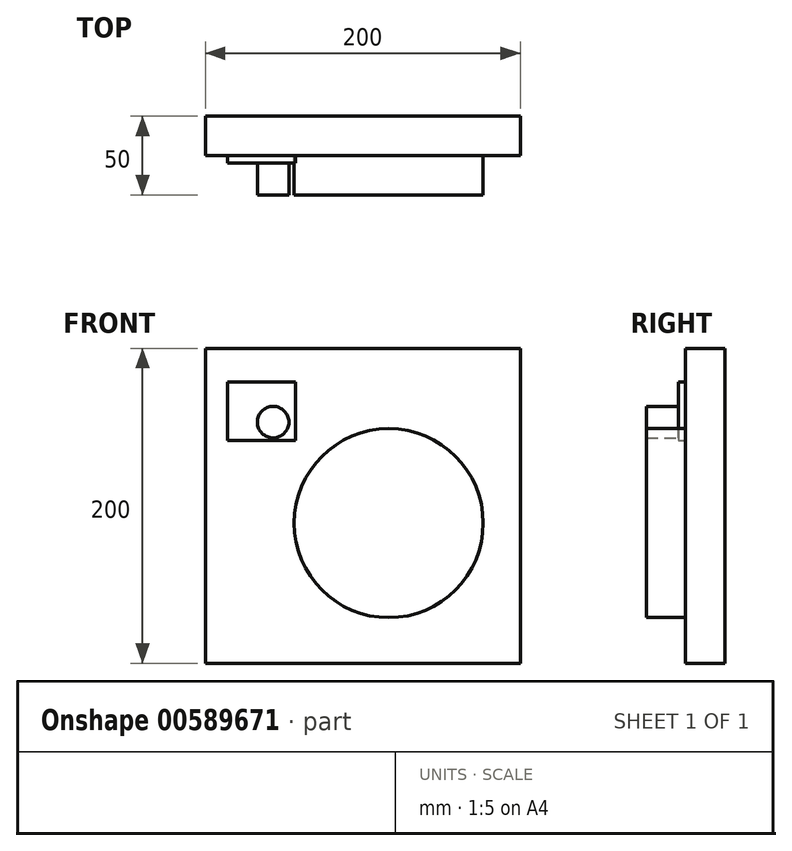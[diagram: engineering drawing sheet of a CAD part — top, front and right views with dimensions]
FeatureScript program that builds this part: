
annotation { "Feature Type Name" : "Feature", "Feature Type Description" : "" }
export const myFeature = defineFeature(function(context is Context, id is Id, definition is map)
    precondition{}
    {
        {
            var Q0;
            Q0=qCreatedBy(makeId("Front.planeOp"),FACE);
            var sketch = newSketch(context, id + "F0", { "sketchPlane" : qUnion([Q0])});
            skLineSegment(sketch, "E0.bottom", {"start": v(-200, -200) * mm, "end": v(0, -200) * mm});
            skLineSegment(sketch, "E0.top", {"start": v(-200, 0) * mm, "end": v(0, 0) * mm});
            skLineSegment(sketch, "E0.left", {"start": v(-200, -200) * mm, "end": v(-200, 0) * mm});
            skLineSegment(sketch, "E0.right", {"start": v(0, -200) * mm, "end": v(0, 0) * mm});
            skSolve(sketch);
        }
        {
            var Q0;
            Q0 = qSketchRegion(id + "F0", true);
            extrude(context, id + "F1", {"entities" : qUnion([Q0]), "depth" : 25 * mm, "offsetDistance" : 25 * mm});
        }
        {
            var Q0;
            Q0=makeQuery(id+"F1.opExtrude","CAP_FACE",FACE,{"disambiguationData":[OSD([sQuery(id+"F0.wireOp",EDGE,"E0.bottom"),sQuery(id+"F0.wireOp",EDGE,"E0.top"),sQuery(id+"F0.wireOp",EDGE,"E0.left"),sQuery(id+"F0.wireOp",EDGE,"E0.right")])],"isStart":false});
            var sketch = newSketch(context, id + "F2", { "sketchPlane" : qUnion([Q0])});
            skCircle(sketch, "E1", {"center": v(-156.98, -46.83) * mm, "radius": 10 * mm});
            skCircle(sketch, "E2", {"center": v(-83.56, -110.98) * mm, "radius": 60 * mm});
            skLineSegment(sketch, "E3", {"start": v(-156.98, -46.83) * mm, "end": v(-83.56, -110.98) * mm});
            skSolve(sketch);
        }
        {
            var Q0;
            Q0 = qSketchRegion(id + "F2", true);
            extrude(context, id + "F3", {"entities" : qUnion([Q0]), "operationType" : NewBodyOperationType.ADD, "depth" : 25 * mm, "offsetDistance" : 25 * mm});
        }
        {
            var Q0;
            Q0=makeQuery(id+"F1.opExtrude","CAP_FACE",FACE,{"disambiguationData":[OSD([sQuery(id+"F0.wireOp",EDGE,"E0.bottom"),sQuery(id+"F0.wireOp",EDGE,"E0.top"),sQuery(id+"F0.wireOp",EDGE,"E0.left"),sQuery(id+"F0.wireOp",EDGE,"E0.right")])],"isStart":false});
            var sketch = newSketch(context, id + "F4", { "sketchPlane" : qUnion([Q0])});
            skLineSegment(sketch, "E4.bottom", {"start": v(-185.77, -21.34) * mm, "end": v(-142.73, -21.34) * mm});
            skLineSegment(sketch, "E4.top", {"start": v(-185.77, -58.5) * mm, "end": v(-142.73, -58.5) * mm});
            skLineSegment(sketch, "E4.left", {"start": v(-185.77, -21.34) * mm, "end": v(-185.77, -58.5) * mm});
            skLineSegment(sketch, "E4.right", {"start": v(-142.73, -21.34) * mm, "end": v(-142.73, -58.5) * mm});
            skSolve(sketch);
        }
        {
            var Q0;
            Q0=makeQuery(id+"F4.imprint","IMPRINT",FACE,{"disambiguationData":[TD([[makeQuery(id+"F4.imprint","IMPRINT",EDGE,{"derivedFrom":sQuery(id+"F4.wireOp",EDGE,"E4.bottom")}),-1.0]])]});
            extrude(context, id + "F5", {"entities" : qUnion([Q0]), "operationType" : NewBodyOperationType.ADD, "depth" : 4.64 * mm, "offsetDistance" : 25 * mm});
        }
    });
